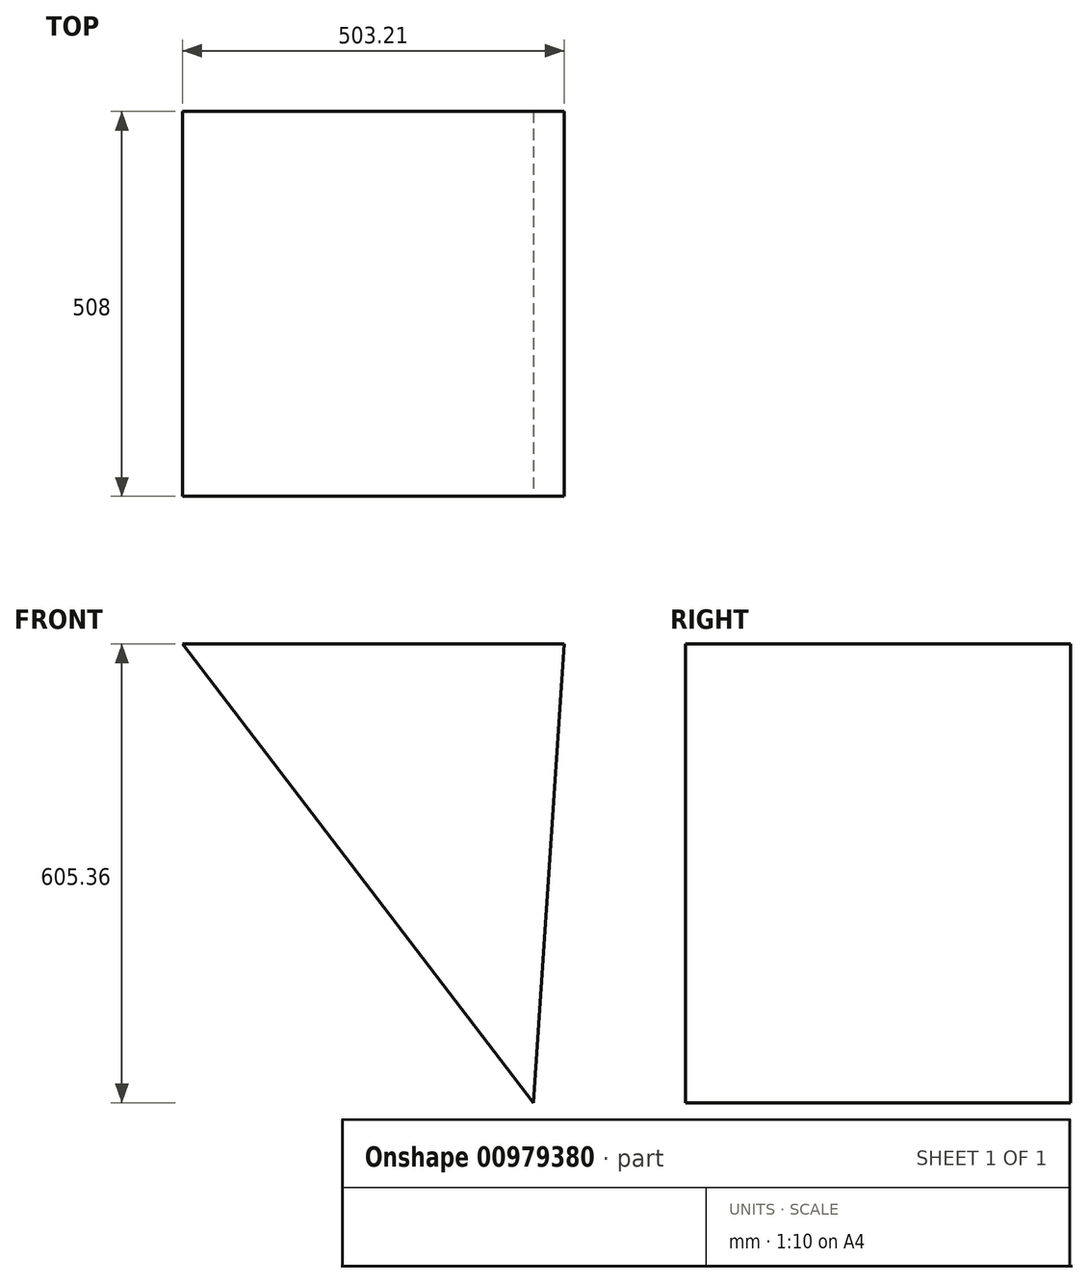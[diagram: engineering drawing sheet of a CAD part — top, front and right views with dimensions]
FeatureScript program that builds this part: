
annotation { "Feature Type Name" : "Feature", "Feature Type Description" : "" }
export const myFeature = defineFeature(function(context is Context, id is Id, definition is map)
    precondition{}
    {
        {
            var Q0;
            Q0=qCreatedBy(makeId("Front.planeOp"),FACE);
            var sketch = newSketch(context, id + "F0", { "sketchPlane" : qUnion([Q0])});
            skLineSegment(sketch, "E0", {"start": v(0, 0) * mm, "end": v(-503.21, 0) * mm});
            skLineSegment(sketch, "E1", {"start": v(-503.21, 0) * mm, "end": v(-40.41, -605.36) * mm});
            skLineSegment(sketch, "E2", {"start": v(-40.41, -605.36) * mm, "end": v(0, 0) * mm});
            skSolve(sketch);
        }
        {
            var Q0;
            Q0 = qSketchRegion(id + "F0", true);
            extrude(context, id + "F1", {"entities" : qUnion([Q0]), "oppositeDirection" : true, "depth" : 508 * mm, "offsetDistance" : 25.4 * mm});
        }
    });
